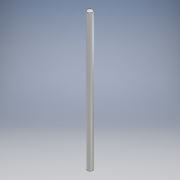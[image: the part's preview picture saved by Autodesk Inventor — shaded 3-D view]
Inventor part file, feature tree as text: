
AUTODESK INVENTOR PART (.ipt)
format: ipt  version: 2017 (Build 210142000, 142)  size: 89,088 bytes
history: native  units: mm
features: extrude x1, sketch x1
ambient origin geometry x8: Origin, YZ Plane, XZ Plane, XY Plane, X Axis, Y Axis, Z Axis, Center Point
bodies: Solid1 (feature_tree)
feature tree (2):
  extrude  "Extrusion1"  Depth=270.0mm TaperAngle=0.0deg
  sketch  "Sketch1"  dims[d0=10.0mm d1=270.0mm d2=0.0mm]
